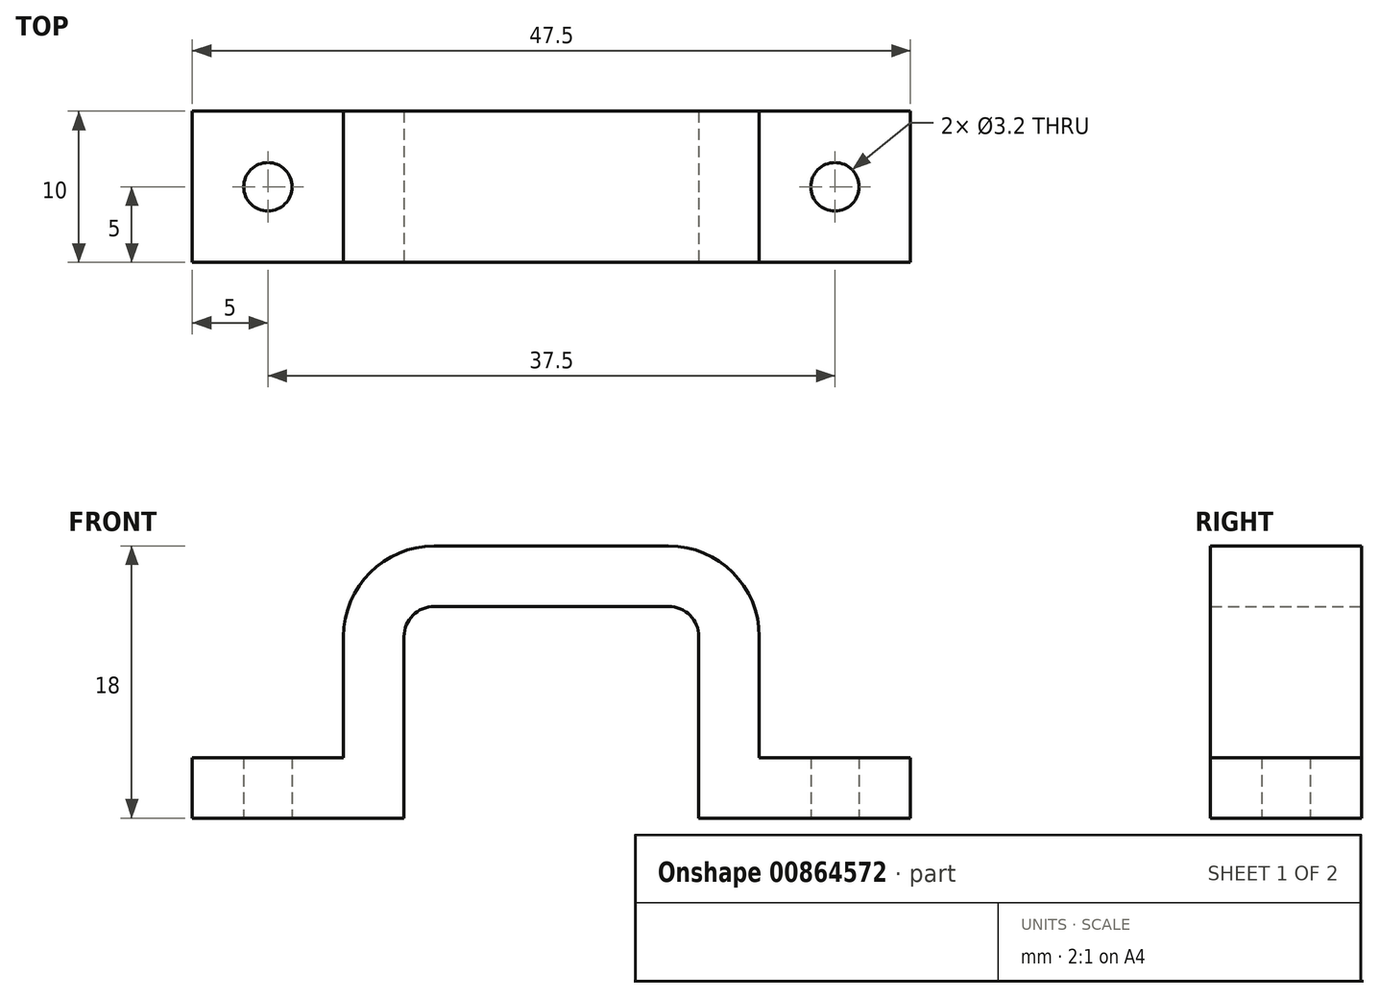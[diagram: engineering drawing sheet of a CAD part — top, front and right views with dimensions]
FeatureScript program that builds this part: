
annotation { "Feature Type Name" : "Feature", "Feature Type Description" : "" }
export const myFeature = defineFeature(function(context is Context, id is Id, definition is map)
    precondition{}
    {
        {
            assignVariable(context, id + "F0", {"name" : "thickness", "anyValue" : 4});
        }
        {
            var Q0;
            Q0=qCreatedBy(makeId("Top.planeOp"),FACE);
            var sketch = newSketch(context, id + "F1", { "sketchPlane" : qUnion([Q0])});
            skLineSegment(sketch, "E0.bottom", {"start": v(23.75, 5) * mm, "end": v(-23.75, 5) * mm});
            skLineSegment(sketch, "E0.top", {"start": v(23.75, -5) * mm, "end": v(-23.75, -5) * mm});
            skLineSegment(sketch, "E0.left", {"start": v(23.75, 5) * mm, "end": v(23.75, -5) * mm});
            skLineSegment(sketch, "E0.right", {"start": v(-23.75, 5) * mm, "end": v(-23.75, -5) * mm});
            skPoint(sketch, "E0.middle", {"position": v(0, 0) * mm});
            skLineSegment(sketch, "E1", {"start": v(-13.75, 5) * mm, "end": v(-13.75, -5) * mm, "construction": true});
            skLineSegment(sketch, "E2", {"start": v(-23.75, 0) * mm, "end": v(-13.75, 0) * mm, "construction": true});
            skCircle(sketch, "E3", {"center": v(-18.75, 0) * mm, "radius": 1.6 * mm});
            skLineSegment(sketch, "E4.MirrorCS", {"start": v(13.75, 5) * mm, "end": v(13.75, -5) * mm, "construction": true});
            skCircle(sketch, "E5.MirrorC", {"center": v(18.75, 0) * mm, "radius": 1.6 * mm});
            skLineSegment(sketch, "E6", {"start": v(-9.75, 5) * mm, "end": v(-9.75, -5) * mm});
            skLineSegment(sketch, "E7.MirrorCS", {"start": v(9.75, 5) * mm, "end": v(9.75, -5) * mm});
            skSolve(sketch);
        }
        {
            var Q0;
            {var subQ0=sQuery(id+"F1.wireOp",EDGE,"E0.right");Q0=makeQuery(id+"F1.imprint","IMPRINT",FACE,{"disambiguationData":[TD([[makeQuery(id+"F1.imprint","IMPRINT",EDGE,{"derivedFrom":subQ0}),1.0]])]});}
            var Q1;
            {var subQ0=sQuery(id+"F1.wireOp",EDGE,"E0.left");Q1=makeQuery(id+"F1.imprint","IMPRINT",FACE,{"disambiguationData":[TD([[makeQuery(id+"F1.imprint","IMPRINT",EDGE,{"derivedFrom":subQ0}),-1.0]])]});}
            extrude(context, id + "F2", {"entities" : qUnion([Q0, Q1]), "depth" : (getVariable(context, 'thickness')) * mm, "offsetDistance" : 25 * mm});
        }
        {
            var Q0;
            Q0=qCreatedBy(makeId("Front.planeOp"),FACE);
            var sketch = newSketch(context, id + "F3", { "sketchPlane" : qUnion([Q0])});
            skLineSegment(sketch, "E8.bottom", {"start": v(-9.75, 0) * mm, "end": v(9.75, 0) * mm});
            skLineSegment(sketch, "E8.top", {"start": v(-7.75, 14) * mm, "end": v(7.75, 14) * mm});
            skLineSegment(sketch, "E8.left", {"start": v(-9.75, 0) * mm, "end": v(-9.75, 12) * mm});
            skLineSegment(sketch, "E8.right", {"start": v(9.75, 0) * mm, "end": v(9.75, 12) * mm});
            skPoint(sketch, "E9.visualSharp", {"position": v(-9.75, 14) * mm});
            skArc(sketch, "E9.filletArc", {"start": v(-7.75, 14) * mm, "mid": v(-9.16, 13.41) * mm, "end": v(-9.75, 12) * mm});
            skPoint(sketch, "E10.visualSharp", {"position": v(9.75, 14) * mm});
            skArc(sketch, "E10.filletArc", {"start": v(9.75, 12) * mm, "mid": v(9.16, 13.41) * mm, "end": v(7.75, 14) * mm});
            skLineSegment(sketch, "E11.0", {"start": v(13.75, 0) * mm, "end": v(13.75, 12) * mm});
            skLineSegment(sketch, "E11.1", {"start": v(-13.75, 0) * mm, "end": v(-13.75, 12) * mm});
            skArc(sketch, "E11.2", {"start": v(-7.75, 18) * mm, "mid": v(-12, 16.24) * mm, "end": v(-13.75, 12) * mm});
            skLineSegment(sketch, "E11.3", {"start": v(-7.75, 18) * mm, "end": v(7.75, 18) * mm});
            skArc(sketch, "E11.4", {"start": v(13.75, 12) * mm, "mid": v(12, 16.24) * mm, "end": v(7.75, 18) * mm});
            skLineSegment(sketch, "E12", {"start": v(-9.75, 0) * mm, "end": v(-13.75, 0) * mm});
            skLineSegment(sketch, "E13", {"start": v(9.75, 0) * mm, "end": v(13.75, 0) * mm});
            skSolve(sketch);
        }
        {
            var Q0;
            Q0=makeQuery(id+"F3.imprint","IMPRINT",FACE,{"disambiguationData":[TD([[makeQuery(id+"F3.imprint","IMPRINT",EDGE,{"derivedFrom":sQuery(id+"F3.wireOp",EDGE,"E8.top")}),1.0]])]});
            var Q1;
            {var subQ0=sQuery(id+"F1.wireOp",EDGE,"E0.top");Q1=makeQuery(id+"F2.opExtrude","SWEPT_FACE",FACE,{"disambiguationData":[OSD([subQ0]),TDD([makeQuery(id+"F1.imprint","IMPRINT",EDGE,{"disambiguationData":[TD([[makeQuery(id+"F1.imprint","INTERSECT",VERTEX,{"derivedFrom":[subQ0,sQuery(id+"F1.wireOp",EDGE,"E0.right")]}),1.0]])],"derivedFrom":subQ0})])]});}
            var Q2;
            {var subQ0=sQuery(id+"F1.wireOp",EDGE,"E0.bottom");Q2=makeQuery(id+"F2.opExtrude","SWEPT_FACE",FACE,{"disambiguationData":[OSD([subQ0]),TDD([makeQuery(id+"F1.imprint","IMPRINT",EDGE,{"disambiguationData":[TD([[makeQuery(id+"F1.imprint","INTERSECT",VERTEX,{"derivedFrom":[subQ0,sQuery(id+"F1.wireOp",EDGE,"E0.left")]}),-1.0]])],"derivedFrom":subQ0})])]});}
            extrude(context, id + "F4", {"entities" : qUnion([Q0]), "operationType" : NewBodyOperationType.ADD, "endBound" : BoundingType.UP_TO_SURFACE, "depth" : 25 * mm, "endBoundEntityFace" : qUnion([Q1]), "offsetDistance" : 25 * mm, "hasSecondDirection" : true, "secondDirectionBound" : BoundingType.UP_TO_SURFACE, "secondDirectionOppositeDirection" : true, "secondDirectionDepth" : 25 * mm, "secondDirectionBoundEntityFace" : qUnion([Q2])});
        }
    });
